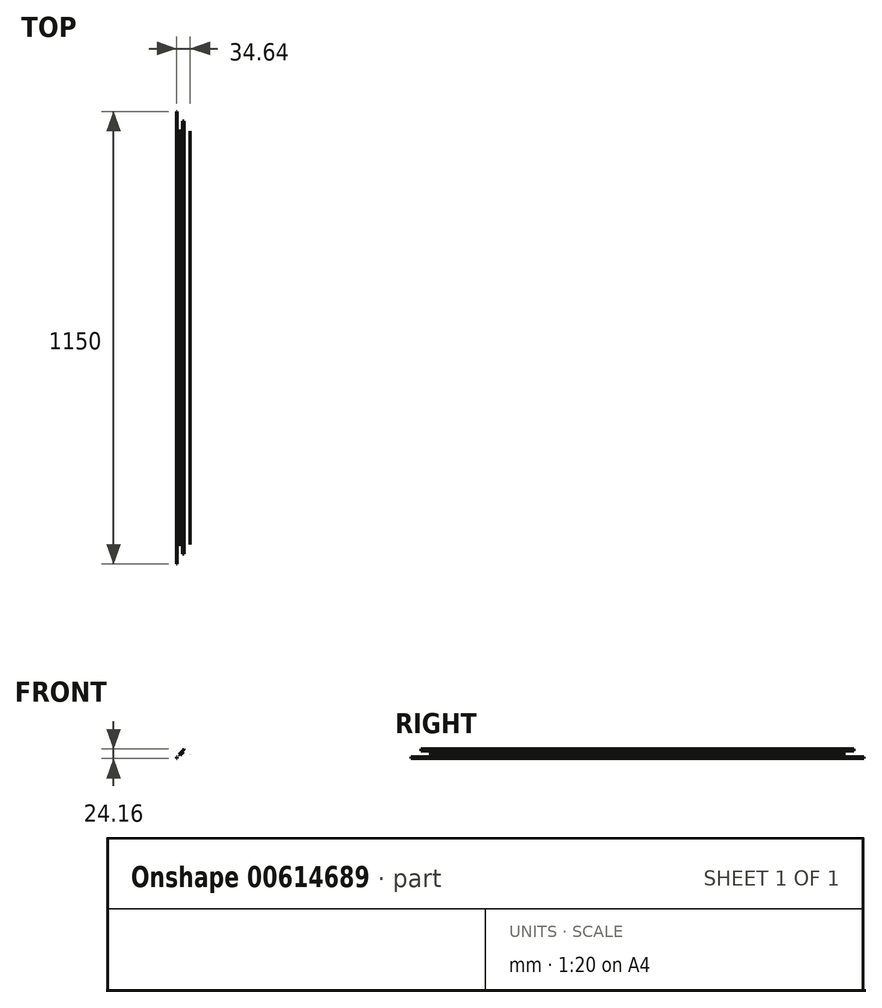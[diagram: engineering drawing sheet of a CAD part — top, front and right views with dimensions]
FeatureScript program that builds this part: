
annotation { "Feature Type Name" : "Feature", "Feature Type Description" : "" }
export const myFeature = defineFeature(function(context is Context, id is Id, definition is map)
    precondition{}
    {
        {
            var Q0;
            Q0=qCreatedBy(makeId("Front.planeOp"),FACE);
            var sketch = newSketch(context, id + "F0", { "sketchPlane" : qUnion([Q0])});
            skLineSegment(sketch, "E0.top", {"start": v(-22.5, -22.5) * mm, "end": v(22.5, -22.5) * mm, "construction": true});
            skLineSegment(sketch, "E0.left", {"start": v(-22.5, 22.5) * mm, "end": v(-22.5, -17.5) * mm, "construction": true});
            skLineSegment(sketch, "E0.right", {"start": v(22.5, 22.5) * mm, "end": v(22.5, -22.5) * mm, "construction": true});
            skPoint(sketch, "E0.middle", {"position": v(0, 0) * mm});
            skLineSegment(sketch, "E1", {"start": v(0, 0) * mm, "end": v(0, 21.4) * mm, "construction": true});
            skLineSegment(sketch, "E2", {"start": v(0, 0) * mm, "end": v(-11.87, 0) * mm, "construction": true});
            skLineSegment(sketch, "E3", {"start": v(0, 0) * mm, "end": v(6.41, 0) * mm, "construction": true});
            skLineSegment(sketch, "E4.top", {"start": v(-17.5, -17.5) * mm, "end": v(17.5, -17.5) * mm, "construction": true});
            skLineSegment(sketch, "E4.left", {"start": v(-17.5, 17.5) * mm, "end": v(-17.5, -14.52) * mm, "construction": true});
            skLineSegment(sketch, "E4.right", {"start": v(17.5, 17.5) * mm, "end": v(17.5, -14.52) * mm, "construction": true});
            skLineSegment(sketch, "E5.top", {"start": v(-19.5, -17.5) * mm, "end": v(22.5, -17.5) * mm, "construction": true});
            skLineSegment(sketch, "E5.left", {"start": v(-22.5, -22.5) * mm, "end": v(-22.5, -17.5) * mm, "construction": true});
            skLineSegment(sketch, "E5.right", {"start": v(22.5, -22.5) * mm, "end": v(22.5, -17.5) * mm, "construction": true});
            skLineSegment(sketch, "E6", {"start": v(-17.5, -17.5) * mm, "end": v(0, 0) * mm, "construction": true});
            skLineSegment(sketch, "E7", {"start": v(0, 0) * mm, "end": v(17.5, -17.5) * mm, "construction": true});
            skLineSegment(sketch, "E8.bottom", {"start": v(17.5, -17.5) * mm, "end": v(17.5, -17.5) * mm, "construction": true});
            skLineSegment(sketch, "E8.left", {"start": v(-17.5, -17.5) * mm, "end": v(-17.5, -22.5) * mm, "construction": true});
            skLineSegment(sketch, "E9.top", {"start": v(-22.5, -12.5) * mm, "end": v(22.5, -12.5) * mm, "construction": true});
            skLineSegment(sketch, "E9.left", {"start": v(-22.5, -17.5) * mm, "end": v(-22.5, -12.5) * mm, "construction": true});
            skLineSegment(sketch, "E9.right", {"start": v(22.5, -17.5) * mm, "end": v(22.5, -12.5) * mm, "construction": true});
            skLineSegment(sketch, "E10.top", {"start": v(-22.5, 5) * mm, "end": v(22.5, 5) * mm, "construction": true});
            skLineSegment(sketch, "E10.left", {"start": v(-22.5, 0) * mm, "end": v(-22.5, 5) * mm, "construction": true});
            skLineSegment(sketch, "E10.right", {"start": v(22.5, 0) * mm, "end": v(22.5, 5) * mm, "construction": true});
            skLineSegment(sketch, "E11", {"start": v(0, 5) * mm, "end": v(-17.5, -12.5) * mm, "construction": true});
            skLineSegment(sketch, "E12", {"start": v(0, 5) * mm, "end": v(17.5, -12.5) * mm, "construction": true});
            skLineSegment(sketch, "E13", {"start": v(0, 5) * mm, "end": v(-14.14, -9.14) * mm});
            skLineSegment(sketch, "E14", {"start": v(0, 5) * mm, "end": v(14.14, -9.14) * mm});
            skLineSegment(sketch, "E15", {"start": v(-14.14, -9.14) * mm, "end": v(-14.85, -8.44) * mm});
            skLineSegment(sketch, "E16", {"start": v(-11.87, -5.46) * mm, "end": v(0, 6.41) * mm});
            skLineSegment(sketch, "E17", {"start": v(14.14, -9.14) * mm, "end": v(14.85, -8.44) * mm});
            skLineSegment(sketch, "E18", {"start": v(11.87, -5.46) * mm, "end": v(0, 6.41) * mm});
            skLineSegment(sketch, "E19", {"start": v(-14.14, -9.14) * mm, "end": v(-11.31, -11.97) * mm});
            skLineSegment(sketch, "E20", {"start": v(-11.31, -11.97) * mm, "end": v(-1.41, -2.07) * mm});
            skLineSegment(sketch, "E21", {"start": v(-1.41, -2.07) * mm, "end": v(-4.24, 0.76) * mm});
            skLineSegment(sketch, "E22", {"start": v(-4.24, 0.76) * mm, "end": v(-14.14, -9.14) * mm});
            skLineSegment(sketch, "E23", {"start": v(14.14, -9.14) * mm, "end": v(11.31, -11.97) * mm});
            skLineSegment(sketch, "E24", {"start": v(11.31, -11.97) * mm, "end": v(1.41, -2.07) * mm});
            skLineSegment(sketch, "E25", {"start": v(1.41, -2.07) * mm, "end": v(4.24, 0.76) * mm});
            skLineSegment(sketch, "E26", {"start": v(4.24, 0.76) * mm, "end": v(14.14, -9.14) * mm});
            skLineSegment(sketch, "E27.top", {"start": v(-17.5, -14.52) * mm, "end": v(17.5, -14.52) * mm, "construction": true});
            skLineSegment(sketch, "E27.left", {"start": v(-17.5, -17.5) * mm, "end": v(-17.5, -14.52) * mm, "construction": true});
            skLineSegment(sketch, "E27.right", {"start": v(17.5, -17.5) * mm, "end": v(17.5, -14.52) * mm, "construction": true});
            skLineSegment(sketch, "E28.bottom", {"start": v(-14.85, -8.44) * mm, "end": v(14.85, -8.44) * mm, "construction": true});
            skLineSegment(sketch, "E28.top", {"start": v(-14.85, -14.52) * mm, "end": v(14.85, -14.52) * mm, "construction": true});
            skLineSegment(sketch, "E28.left", {"start": v(-14.85, -8.44) * mm, "end": v(-14.85, -14.52) * mm, "construction": true});
            skLineSegment(sketch, "E28.right", {"start": v(14.85, -8.44) * mm, "end": v(14.85, -14.52) * mm, "construction": true});
            skLineSegment(sketch, "E29.top", {"start": v(-14.85, -5.46) * mm, "end": v(14.85, -5.46) * mm, "construction": true});
            skLineSegment(sketch, "E29.left", {"start": v(-14.85, -8.44) * mm, "end": v(-14.85, -5.46) * mm, "construction": true});
            skLineSegment(sketch, "E29.right", {"start": v(14.85, -8.44) * mm, "end": v(14.85, -5.46) * mm, "construction": true});
            skLineSegment(sketch, "E30.top", {"start": v(-14.85, 0) * mm, "end": v(6.41, 0) * mm, "construction": true});
            skLineSegment(sketch, "E30.left", {"start": v(-14.85, -5.46) * mm, "end": v(-14.85, 0) * mm, "construction": true});
            skLineSegment(sketch, "E30.right", {"start": v(14.85, -5.46) * mm, "end": v(14.85, 0) * mm, "construction": true});
            skLineSegment(sketch, "E31.bottom", {"start": v(-11.87, -5.46) * mm, "end": v(11.85, -5.46) * mm, "construction": true});
            skLineSegment(sketch, "E31.top", {"start": v(-6.41, 0) * mm, "end": v(6.41, 0) * mm, "construction": true});
            skLineSegment(sketch, "E31.left", {"start": v(-11.87, -5.46) * mm, "end": v(-11.87, 0) * mm, "construction": true});
            skLineSegment(sketch, "E31.right", {"start": v(11.85, -5.46) * mm, "end": v(11.85, -5.44) * mm, "construction": true});
            skLineSegment(sketch, "E32.bottom", {"start": v(-6.41, 0) * mm, "end": v(-1.41, 0) * mm, "construction": true});
            skLineSegment(sketch, "E32.top", {"start": v(-6.41, 5) * mm, "end": v(-1.41, 5) * mm, "construction": true});
            skLineSegment(sketch, "E32.left", {"start": v(-6.41, 0) * mm, "end": v(-6.41, 5) * mm, "construction": true});
            skLineSegment(sketch, "E32.right", {"start": v(-1.41, 0) * mm, "end": v(-1.41, 5) * mm, "construction": true});
            skLineSegment(sketch, "E33.bottom", {"start": v(1.41, 5) * mm, "end": v(6.41, 5) * mm, "construction": true});
            skLineSegment(sketch, "E33.top", {"start": v(1.41, 0) * mm, "end": v(6.41, 0) * mm, "construction": true});
            skLineSegment(sketch, "E33.left", {"start": v(1.41, 5) * mm, "end": v(1.41, 0) * mm, "construction": true});
            skLineSegment(sketch, "E33.right", {"start": v(6.41, 5) * mm, "end": v(6.41, 0) * mm, "construction": true});
            skLineSegment(sketch, "E34.bottom", {"start": v(-1.41, 5) * mm, "end": v(1.41, 5) * mm, "construction": true});
            skLineSegment(sketch, "E34.top", {"start": v(-1.41, 0) * mm, "end": v(1.41, 0) * mm, "construction": true});
            skLineSegment(sketch, "E34.left", {"start": v(-1.41, 5) * mm, "end": v(-1.41, 0) * mm, "construction": true});
            skLineSegment(sketch, "E35", {"start": v(-22.5, -22.5) * mm, "end": v(-17.5, -22.5) * mm, "construction": true});
            skLineSegment(sketch, "E36", {"start": v(-17.5, -14.52) * mm, "end": v(-14.85, -14.52) * mm, "construction": true});
            skLineSegment(sketch, "E37", {"start": v(-6.41, 0) * mm, "end": v(0, 6.41) * mm});
            skLineSegment(sketch, "E38", {"start": v(14.85, -14.52) * mm, "end": v(17.5, -14.52) * mm});
            skLineSegment(sketch, "E39", {"start": v(-14.85, -8.44) * mm, "end": v(-11.87, -5.46) * mm});
            skLineSegment(sketch, "E40", {"start": v(0, 6.41) * mm, "end": v(6.41, 0) * mm});
            skLineSegment(sketch, "E41", {"start": v(11.85, -5.44) * mm, "end": v(11.85, -5.46) * mm});
            skPoint(sketch, "E42.start.orphan", {"position": v(29.54, 0) * mm});
            skLineSegment(sketch, "E43", {"start": v(0, 6.41) * mm, "end": v(-22.5, 6.41) * mm, "construction": true});
            skLineSegment(sketch, "E44", {"start": v(0, 6.41) * mm, "end": v(22.5, 6.41) * mm, "construction": true});
            skLineSegment(sketch, "E45", {"start": v(0, 6.41) * mm, "end": v(0, 21.38) * mm, "construction": true});
            skLineSegment(sketch, "E46.trimOffspring", {"start": v(-14.85, 0) * mm, "end": v(-22.5, 0) * mm, "construction": true});
            skLineSegment(sketch, "E47.trimOffspring", {"start": v(11.85, 0) * mm, "end": v(22.5, 0) * mm, "construction": true});
            skLineSegment(sketch, "E48.trimOffspring", {"start": v(11.85, 0) * mm, "end": v(14.85, 0) * mm, "construction": true});
            skLineSegment(sketch, "E49.bottom", {"start": v(22.5, -17.5) * mm, "end": v(-19.5, -17.5) * mm, "construction": true});
            skLineSegment(sketch, "E49.top", {"start": v(22.5, -19.5) * mm, "end": v(19.5, -19.5) * mm, "construction": true});
            skLineSegment(sketch, "E49.left", {"start": v(22.5, -17.5) * mm, "end": v(22.5, -19.5) * mm, "construction": true});
            skLineSegment(sketch, "E49.right", {"start": v(-22.5, -17.5) * mm, "end": v(-22.5, -19.5) * mm, "construction": true});
            skLineSegment(sketch, "E50.top", {"start": v(-22.5, 25.5) * mm, "end": v(-18.5, 25.5) * mm, "construction": true});
            skLineSegment(sketch, "E50.left", {"start": v(-22.5, 22.5) * mm, "end": v(-22.5, 25.5) * mm, "construction": true});
            skLineSegment(sketch, "E50.right", {"start": v(22.5, 22.5) * mm, "end": v(22.5, 25.5) * mm, "construction": true});
            skLineSegment(sketch, "E51.top", {"start": v(-22.5, -19.5) * mm, "end": v(17.5, -19.5) * mm, "construction": true});
            skLineSegment(sketch, "E51.left", {"start": v(-22.5, 25.5) * mm, "end": v(-22.5, -19.5) * mm, "construction": true});
            skLineSegment(sketch, "E51.right", {"start": v(22.5, 25.5) * mm, "end": v(22.5, -19.5) * mm, "construction": true});
            skLineSegment(sketch, "E52.bottom", {"start": v(-22.5, 6.41) * mm, "end": v(-18.5, 6.41) * mm, "construction": true});
            skLineSegment(sketch, "E52.top", {"start": v(-22.5, 28.72) * mm, "end": v(-18.5, 28.72) * mm, "construction": true});
            skLineSegment(sketch, "E52.left", {"start": v(-22.5, 6.41) * mm, "end": v(-22.5, 28.72) * mm, "construction": true});
            skLineSegment(sketch, "E52.right", {"start": v(-18.5, 22.5) * mm, "end": v(-18.5, 28.72) * mm, "construction": true});
            skLineSegment(sketch, "E53.bottom", {"start": v(22.5, 6.41) * mm, "end": v(18.5, 6.41) * mm, "construction": true});
            skLineSegment(sketch, "E53.top", {"start": v(22.5, 28.29) * mm, "end": v(18.5, 28.29) * mm, "construction": true});
            skLineSegment(sketch, "E53.left", {"start": v(22.5, 6.41) * mm, "end": v(22.5, 28.29) * mm, "construction": true});
            skLineSegment(sketch, "E53.right", {"start": v(18.5, 6.41) * mm, "end": v(18.5, 28.29) * mm, "construction": true});
            skLineSegment(sketch, "E54.bottom", {"start": v(-18.5, 6.41) * mm, "end": v(18.5, 6.41) * mm, "construction": true});
            skLineSegment(sketch, "E54.left", {"start": v(-18.5, 6.41) * mm, "end": v(-18.5, 21.4) * mm, "construction": true});
            skLineSegment(sketch, "E55.top", {"start": v(-18.5, 21.4) * mm, "end": v(18.5, 21.4) * mm, "construction": true});
            skLineSegment(sketch, "E55.right", {"start": v(18.5, 6.41) * mm, "end": v(18.5, 21.4) * mm, "construction": true});
            skPoint(sketch, "E56.orphan", {"position": v(0, 22.5) * mm});
            skLineSegment(sketch, "E57.bottom", {"start": v(-22.5, -19.5) * mm, "end": v(-24.5, -19.5) * mm, "construction": true});
            skLineSegment(sketch, "E57.top", {"start": v(-22.5, 25.5) * mm, "end": v(-24.5, 25.5) * mm, "construction": true});
            skLineSegment(sketch, "E57.left", {"start": v(-22.5, -19.5) * mm, "end": v(-22.5, 25.5) * mm, "construction": true});
            skLineSegment(sketch, "E57.right", {"start": v(-24.5, -19.5) * mm, "end": v(-24.5, 25.5) * mm, "construction": true});
            skLineSegment(sketch, "E58.bottom", {"start": v(22.5, -19.5) * mm, "end": v(24.5, -19.5) * mm, "construction": true});
            skLineSegment(sketch, "E58.top", {"start": v(22.5, 25.5) * mm, "end": v(24.5, 25.5) * mm, "construction": true});
            skLineSegment(sketch, "E58.left", {"start": v(22.5, -19.5) * mm, "end": v(22.5, 25.5) * mm, "construction": true});
            skLineSegment(sketch, "E58.right", {"start": v(24.5, -19.5) * mm, "end": v(24.5, 25.5) * mm, "construction": true});
            skLineSegment(sketch, "E59.bottom", {"start": v(-17.5, -17.5) * mm, "end": v(-19.5, -17.5) * mm, "construction": true});
            skLineSegment(sketch, "E59.top", {"start": v(-17.5, -14.52) * mm, "end": v(-19.5, -14.52) * mm, "construction": true});
            skLineSegment(sketch, "E59.right", {"start": v(-19.5, -17.5) * mm, "end": v(-19.5, -14.52) * mm, "construction": true});
            skLineSegment(sketch, "E60.bottom", {"start": v(17.5, -17.5) * mm, "end": v(19.5, -17.5) * mm, "construction": true});
            skLineSegment(sketch, "E60.top", {"start": v(17.5, -14.52) * mm, "end": v(19.5, -14.52) * mm, "construction": true});
            skLineSegment(sketch, "E60.right", {"start": v(19.5, -17.5) * mm, "end": v(19.5, -14.52) * mm, "construction": true});
            skLineSegment(sketch, "E61", {"start": v(-22.5, 6.41) * mm, "end": v(-24.5, 6.41) * mm, "construction": true});
            skLineSegment(sketch, "E62", {"start": v(22.5, 6.41) * mm, "end": v(24.5, 6.41) * mm, "construction": true});
            skLineSegment(sketch, "E63.bottom", {"start": v(-22.5, -19.5) * mm, "end": v(-19.5, -19.5) * mm, "construction": true});
            skLineSegment(sketch, "E63.top", {"start": v(-22.5, -17.5) * mm, "end": v(-19.5, -17.5) * mm, "construction": true});
            skLineSegment(sketch, "E63.left", {"start": v(-22.5, -19.5) * mm, "end": v(-22.5, -17.5) * mm, "construction": true});
            skLineSegment(sketch, "E63.right", {"start": v(-19.5, -19.5) * mm, "end": v(-19.5, -17.5) * mm, "construction": true});
            skLineSegment(sketch, "E64.top", {"start": v(22.5, -17.5) * mm, "end": v(19.5, -17.5) * mm, "construction": true});
            skLineSegment(sketch, "E64.left", {"start": v(22.5, -19.5) * mm, "end": v(22.5, -17.5) * mm, "construction": true});
            skLineSegment(sketch, "E64.right", {"start": v(19.5, -19.5) * mm, "end": v(19.5, -17.5) * mm, "construction": true});
            skLineSegment(sketch, "E65.bottom", {"start": v(-18.5, 21.4) * mm, "end": v(-24.5, 21.4) * mm, "construction": true});
            skLineSegment(sketch, "E65.top", {"start": v(-18.5, 25.5) * mm, "end": v(-24.5, 25.5) * mm, "construction": true});
            skLineSegment(sketch, "E65.left", {"start": v(-18.5, 21.4) * mm, "end": v(-18.5, 25.5) * mm, "construction": true});
            skLineSegment(sketch, "E65.right", {"start": v(-24.5, 21.4) * mm, "end": v(-24.5, 25.5) * mm, "construction": true});
            skLineSegment(sketch, "E66.bottom", {"start": v(18.5, 21.4) * mm, "end": v(24.5, 21.4) * mm, "construction": true});
            skLineSegment(sketch, "E66.left", {"start": v(18.5, 21.4) * mm, "end": v(18.5, 25.5) * mm, "construction": true});
            skLineSegment(sketch, "E66.right", {"start": v(24.5, 21.4) * mm, "end": v(24.5, 25.5) * mm, "construction": true});
            skLineSegment(sketch, "E67", {"start": v(-24.5, 6.41) * mm, "end": v(-24.5, -17.57) * mm});
            skLineSegment(sketch, "E68", {"start": v(-19.5, -17.5) * mm, "end": v(-19.5, -14.52) * mm});
            skLineSegment(sketch, "E69", {"start": v(-19.5, -14.52) * mm, "end": v(-14.85, -14.52) * mm});
            skLineSegment(sketch, "E70", {"start": v(-14.85, -14.52) * mm, "end": v(-14.85, -8.44) * mm});
            skLineSegment(sketch, "E71", {"start": v(-11.87, -5.46) * mm, "end": v(-11.87, 0) * mm});
            skLineSegment(sketch, "E72", {"start": v(-11.87, 0) * mm, "end": v(-6.41, 0) * mm});
            skLineSegment(sketch, "E73", {"start": v(11.85, -5.44) * mm, "end": v(11.87, -5.46) * mm});
            skLineSegment(sketch, "E74", {"start": v(14.85, -8.44) * mm, "end": v(14.85, -14.06) * mm});
            skLineSegment(sketch, "E75", {"start": v(14.85, -14.06) * mm, "end": v(14.85, -14.52) * mm});
            skLineSegment(sketch, "E76", {"start": v(17.5, -14.52) * mm, "end": v(17.5, -17.5) * mm});
            skLineSegment(sketch, "E77", {"start": v(17.5, -19.5) * mm, "end": v(22.5, -19.5) * mm});
            skLineSegment(sketch, "E78", {"start": v(22.5, -19.5) * mm, "end": v(22.5, 6.41) * mm});
            skLineSegment(sketch, "E79", {"start": v(18.5, 25.5) * mm, "end": v(-22.5, 25.5) * mm});
            skLineSegment(sketch, "E80", {"start": v(-24.5, -17.57) * mm, "end": v(-24.5, -19.5) * mm});
            skLineSegment(sketch, "E81", {"start": v(-24.5, -19.5) * mm, "end": v(-19.5, -19.5) * mm});
            skLineSegment(sketch, "E82", {"start": v(-19.5, -19.5) * mm, "end": v(-19.5, -17.5) * mm});
            skLineSegment(sketch, "E83", {"start": v(18.5, 25.5) * mm, "end": v(22.5, 25.5) * mm});
            skLineSegment(sketch, "E84", {"start": v(24.5, 6.41) * mm, "end": v(24.5, -19.5) * mm});
            skLineSegment(sketch, "E85", {"start": v(24.5, -19.5) * mm, "end": v(22.5, -19.5) * mm});
            skLineSegment(sketch, "E86.trimOffspring", {"start": v(17.5, -19.5) * mm, "end": v(-22.5, -19.5) * mm, "construction": true});
            skLineSegment(sketch, "E87", {"start": v(14.85, -14.52) * mm, "end": v(19.5, -14.52) * mm});
            skLineSegment(sketch, "E88", {"start": v(19.5, -14.52) * mm, "end": v(19.5, -19.5) * mm});
            skLineSegment(sketch, "E89", {"start": v(19.5, -19.5) * mm, "end": v(24.5, -19.5) * mm});
            skLineSegment(sketch, "E90.trimOffspring", {"start": v(19.5, -19.5) * mm, "end": v(22.5, -19.5) * mm, "construction": true});
            skLineSegment(sketch, "E91.bottom", {"start": v(-24.5, 25.5) * mm, "end": v(24.5, 25.5) * mm, "construction": true});
            skLineSegment(sketch, "E91.top", {"start": v(-24.5, 0) * mm, "end": v(6.41, 0) * mm, "construction": true});
            skLineSegment(sketch, "E91.left", {"start": v(-24.5, 25.5) * mm, "end": v(-24.5, 0) * mm, "construction": true});
            skLineSegment(sketch, "E91.right", {"start": v(24.5, 25.5) * mm, "end": v(24.5, 0) * mm, "construction": true});
            skLineSegment(sketch, "E92", {"start": v(-22.5, 25.5) * mm, "end": v(-24.5, 0) * mm});
            skLineSegment(sketch, "E93", {"start": v(22.5, 25.5) * mm, "end": v(24.5, 0) * mm});
            skLineSegment(sketch, "E94.top", {"start": v(-22.5, 29.5) * mm, "end": v(22.5, 29.5) * mm, "construction": true});
            skLineSegment(sketch, "E94.left", {"start": v(-22.5, 25.5) * mm, "end": v(-22.5, 29.5) * mm, "construction": true});
            skLineSegment(sketch, "E94.right", {"start": v(22.5, 25.5) * mm, "end": v(22.5, 29.5) * mm, "construction": true});
            skLineSegment(sketch, "E95", {"start": v(-22.5, 25.5) * mm, "end": v(-18.5, 29.5) * mm});
            skLineSegment(sketch, "E96", {"start": v(22.5, 25.5) * mm, "end": v(18.49, 29.5) * mm});
            skLineSegment(sketch, "E97", {"start": v(18.49, 29.5) * mm, "end": v(-18.94, 29.5) * mm});
            skLineSegment(sketch, "E98.trimOffspring", {"start": v(18.5, 25.5) * mm, "end": v(22.5, 25.5) * mm, "construction": true});
            skLineSegment(sketch, "E99", {"start": v(11.85, -5.44) * mm, "end": v(14.85, -8.44) * mm});
            skLineSegment(sketch, "E100", {"start": v(14.85, -8.44) * mm, "end": v(14.85, -14.52) * mm});
            skLineSegment(sketch, "E101.trimOffspring", {"start": v(11.85, 0) * mm, "end": v(24.5, 0) * mm, "construction": true});
            skLineSegment(sketch, "E102", {"start": v(14.85, -8.44) * mm, "end": v(11.87, -5.46) * mm});
            skLineSegment(sketch, "E103", {"start": v(11.87, -5.46) * mm, "end": v(11.85, 0) * mm});
            skLineSegment(sketch, "E104", {"start": v(11.85, 0) * mm, "end": v(6.41, 0) * mm});
            skLineSegment(sketch, "E105", {"start": v(6.41, 0) * mm, "end": v(1.41, 5) * mm});
            skLineSegment(sketch, "E106.bottom", {"start": v(0, 6.41) * mm, "end": v(-1.41, 6.41) * mm, "construction": true});
            skLineSegment(sketch, "E106.top", {"start": v(0, 5) * mm, "end": v(-1.41, 5) * mm, "construction": true});
            skLineSegment(sketch, "E106.left", {"start": v(0, 6.41) * mm, "end": v(0, 5) * mm, "construction": true});
            skLineSegment(sketch, "E106.right", {"start": v(-1.41, 6.41) * mm, "end": v(-1.41, 5) * mm, "construction": true});
            skLineSegment(sketch, "E107.bottom", {"start": v(0, 6.41) * mm, "end": v(1.41, 6.41) * mm, "construction": true});
            skLineSegment(sketch, "E107.top", {"start": v(0, 5) * mm, "end": v(1.41, 5) * mm, "construction": true});
            skLineSegment(sketch, "E107.right", {"start": v(1.41, 6.41) * mm, "end": v(1.41, 5) * mm, "construction": true});
            skLineSegment(sketch, "E108.bottom", {"start": v(-1.41, 6.41) * mm, "end": v(1.41, 6.41) * mm, "construction": true});
            skLineSegment(sketch, "E108.top", {"start": v(-1.41, 21.4) * mm, "end": v(1.41, 21.4) * mm, "construction": true});
            skLineSegment(sketch, "E108.left", {"start": v(-1.41, 6.41) * mm, "end": v(-1.41, 21.4) * mm, "construction": true});
            skLineSegment(sketch, "E108.right", {"start": v(1.41, 6.41) * mm, "end": v(1.41, 21.4) * mm, "construction": true});
            skLineSegment(sketch, "E109.bottom", {"start": v(1.41, 21.4) * mm, "end": v(-1.41, 21.4) * mm, "construction": true});
            skLineSegment(sketch, "E109.top", {"start": v(1.41, 29.5) * mm, "end": v(-1.41, 29.5) * mm, "construction": true});
            skLineSegment(sketch, "E109.left", {"start": v(1.41, 21.4) * mm, "end": v(1.41, 29.5) * mm, "construction": true});
            skLineSegment(sketch, "E109.right", {"start": v(-1.41, 21.4) * mm, "end": v(-1.41, 29.5) * mm, "construction": true});
            skLineSegment(sketch, "E110", {"start": v(0, 29.5) * mm, "end": v(0, 21.4) * mm});
            skLineSegment(sketch, "E111", {"start": v(0, 21.4) * mm, "end": v(0, 6.41) * mm});
            skLineSegment(sketch, "E112", {"start": v(0, 6.41) * mm, "end": v(-1.41, 6.41) * mm});
            skLineSegment(sketch, "E113", {"start": v(-1.41, 6.41) * mm, "end": v(-1.41, 5) * mm});
            skLineSegment(sketch, "E114", {"start": v(0, 6.41) * mm, "end": v(1.41, 6.41) * mm});
            skLineSegment(sketch, "E115", {"start": v(1.41, 6.41) * mm, "end": v(1.41, 5) * mm});
            skLineSegment(sketch, "E116.top", {"start": v(-23.5, -22.85) * mm, "end": v(21.5, -22.85) * mm, "construction": true});
            skLineSegment(sketch, "E116.left", {"start": v(-23.5, 22.15) * mm, "end": v(-23.5, -17.85) * mm, "construction": true});
            skLineSegment(sketch, "E116.right", {"start": v(21.5, 22.15) * mm, "end": v(21.5, -22.85) * mm, "construction": true});
            skPoint(sketch, "E116.middle", {"position": v(-1, -0.35) * mm});
            skLineSegment(sketch, "E117", {"start": v(-1, -0.35) * mm, "end": v(-1, 21.04) * mm, "construction": true});
            skLineSegment(sketch, "E118", {"start": v(-1, -0.35) * mm, "end": v(-12.87, -0.35) * mm, "construction": true});
            skLineSegment(sketch, "E119", {"start": v(-1, -0.35) * mm, "end": v(5.42, -0.35) * mm, "construction": true});
            skLineSegment(sketch, "E120.top", {"start": v(-18.5, -17.85) * mm, "end": v(16.5, -17.85) * mm, "construction": true});
            skLineSegment(sketch, "E120.left", {"start": v(-18.5, 17.15) * mm, "end": v(-18.5, -14.87) * mm, "construction": true});
            skLineSegment(sketch, "E120.right", {"start": v(16.5, 17.15) * mm, "end": v(16.5, -14.87) * mm, "construction": true});
            skLineSegment(sketch, "E121.top", {"start": v(-20.5, -17.85) * mm, "end": v(21.5, -17.85) * mm, "construction": true});
            skLineSegment(sketch, "E121.left", {"start": v(-23.5, -22.85) * mm, "end": v(-23.5, -17.85) * mm, "construction": true});
            skLineSegment(sketch, "E121.right", {"start": v(21.5, -22.85) * mm, "end": v(21.5, -17.85) * mm, "construction": true});
            skLineSegment(sketch, "E122", {"start": v(-18.5, -17.85) * mm, "end": v(-1, -0.35) * mm, "construction": true});
            skLineSegment(sketch, "E123", {"start": v(-1, -0.35) * mm, "end": v(16.5, -17.85) * mm, "construction": true});
            skLineSegment(sketch, "E124.bottom", {"start": v(16.5, -17.85) * mm, "end": v(16.5, -17.85) * mm, "construction": true});
            skLineSegment(sketch, "E124.left", {"start": v(-18.5, -17.85) * mm, "end": v(-18.5, -22.85) * mm, "construction": true});
            skLineSegment(sketch, "E125.top", {"start": v(-23.5, -12.85) * mm, "end": v(21.5, -12.85) * mm, "construction": true});
            skLineSegment(sketch, "E125.left", {"start": v(-23.5, -17.85) * mm, "end": v(-23.5, -12.85) * mm, "construction": true});
            skLineSegment(sketch, "E125.right", {"start": v(21.5, -17.85) * mm, "end": v(21.5, -12.85) * mm, "construction": true});
            skLineSegment(sketch, "E126.top", {"start": v(-23.5, 4.65) * mm, "end": v(21.5, 4.65) * mm, "construction": true});
            skLineSegment(sketch, "E126.left", {"start": v(-23.5, -0.35) * mm, "end": v(-23.5, 4.65) * mm, "construction": true});
            skLineSegment(sketch, "E126.right", {"start": v(21.5, -0.35) * mm, "end": v(21.5, 4.65) * mm, "construction": true});
            skLineSegment(sketch, "E127", {"start": v(-1, 4.65) * mm, "end": v(-18.5, -12.85) * mm, "construction": true});
            skLineSegment(sketch, "E128", {"start": v(-1, 4.65) * mm, "end": v(16.5, -12.85) * mm, "construction": true});
            skLineSegment(sketch, "E129", {"start": v(-1, 4.65) * mm, "end": v(-15.14, -9.5) * mm});
            skLineSegment(sketch, "E130", {"start": v(-1, 4.65) * mm, "end": v(13.14, -9.5) * mm});
            skLineSegment(sketch, "E131", {"start": v(-15.14, -9.5) * mm, "end": v(-15.85, -8.79) * mm});
            skLineSegment(sketch, "E132", {"start": v(-12.87, -5.81) * mm, "end": v(-1, 6.06) * mm});
            skLineSegment(sketch, "E133", {"start": v(13.14, -9.5) * mm, "end": v(13.85, -8.79) * mm});
            skLineSegment(sketch, "E134", {"start": v(10.87, -5.81) * mm, "end": v(-1, 6.06) * mm});
            skLineSegment(sketch, "E135", {"start": v(-15.14, -9.5) * mm, "end": v(-12.31, -12.32) * mm});
            skLineSegment(sketch, "E136", {"start": v(-12.31, -12.32) * mm, "end": v(-2.41, -2.42) * mm});
            skLineSegment(sketch, "E137", {"start": v(-2.41, -2.42) * mm, "end": v(-5.24, 0.4) * mm});
            skLineSegment(sketch, "E138", {"start": v(-5.24, 0.4) * mm, "end": v(-15.14, -9.5) * mm});
            skLineSegment(sketch, "E139", {"start": v(13.14, -9.5) * mm, "end": v(10.32, -12.32) * mm});
            skLineSegment(sketch, "E140", {"start": v(10.32, -12.32) * mm, "end": v(0.42, -2.42) * mm});
            skLineSegment(sketch, "E141", {"start": v(0.42, -2.42) * mm, "end": v(3.24, 0.4) * mm});
            skLineSegment(sketch, "E142", {"start": v(3.24, 0.4) * mm, "end": v(13.14, -9.5) * mm});
            skLineSegment(sketch, "E143.top", {"start": v(-18.5, -14.87) * mm, "end": v(16.5, -14.87) * mm, "construction": true});
            skLineSegment(sketch, "E143.left", {"start": v(-18.5, -17.85) * mm, "end": v(-18.5, -14.87) * mm, "construction": true});
            skLineSegment(sketch, "E143.right", {"start": v(16.5, -17.85) * mm, "end": v(16.5, -14.87) * mm, "construction": true});
            skLineSegment(sketch, "E144.bottom", {"start": v(-15.85, -8.79) * mm, "end": v(13.85, -8.79) * mm, "construction": true});
            skLineSegment(sketch, "E144.top", {"start": v(-15.85, -14.87) * mm, "end": v(13.85, -14.87) * mm, "construction": true});
            skLineSegment(sketch, "E144.left", {"start": v(-15.85, -8.79) * mm, "end": v(-15.85, -14.87) * mm, "construction": true});
            skLineSegment(sketch, "E144.right", {"start": v(13.85, -8.79) * mm, "end": v(13.85, -14.87) * mm, "construction": true});
            skLineSegment(sketch, "E145.top", {"start": v(-15.85, -5.81) * mm, "end": v(13.85, -5.81) * mm, "construction": true});
            skLineSegment(sketch, "E145.left", {"start": v(-15.85, -8.79) * mm, "end": v(-15.85, -5.81) * mm, "construction": true});
            skLineSegment(sketch, "E145.right", {"start": v(13.85, -8.79) * mm, "end": v(13.85, -5.81) * mm, "construction": true});
            skLineSegment(sketch, "E146.top", {"start": v(-15.85, -0.35) * mm, "end": v(5.42, -0.35) * mm, "construction": true});
            skLineSegment(sketch, "E146.left", {"start": v(-15.85, -5.81) * mm, "end": v(-15.85, -0.35) * mm, "construction": true});
            skLineSegment(sketch, "E146.right", {"start": v(13.85, -5.81) * mm, "end": v(13.85, -0.35) * mm, "construction": true});
            skLineSegment(sketch, "E147.bottom", {"start": v(-12.87, -5.81) * mm, "end": v(10.85, -5.81) * mm, "construction": true});
            skLineSegment(sketch, "E147.top", {"start": v(-7.41, -0.35) * mm, "end": v(5.42, -0.35) * mm, "construction": true});
            skLineSegment(sketch, "E147.left", {"start": v(-12.87, -5.81) * mm, "end": v(-12.87, -0.35) * mm, "construction": true});
            skLineSegment(sketch, "E147.right", {"start": v(10.85, -5.81) * mm, "end": v(10.85, -5.79) * mm, "construction": true});
            skLineSegment(sketch, "E148.bottom", {"start": v(-7.41, -0.35) * mm, "end": v(-2.41, -0.35) * mm, "construction": true});
            skLineSegment(sketch, "E148.top", {"start": v(-7.41, 4.65) * mm, "end": v(-2.41, 4.65) * mm, "construction": true});
            skLineSegment(sketch, "E148.left", {"start": v(-7.41, -0.35) * mm, "end": v(-7.41, 4.65) * mm, "construction": true});
            skLineSegment(sketch, "E148.right", {"start": v(-2.41, -0.35) * mm, "end": v(-2.41, 4.65) * mm, "construction": true});
            skLineSegment(sketch, "E149.bottom", {"start": v(0.42, 4.65) * mm, "end": v(5.42, 4.65) * mm, "construction": true});
            skLineSegment(sketch, "E149.top", {"start": v(0.42, -0.35) * mm, "end": v(5.42, -0.35) * mm, "construction": true});
            skLineSegment(sketch, "E149.left", {"start": v(0.42, 4.65) * mm, "end": v(0.42, -0.35) * mm, "construction": true});
            skLineSegment(sketch, "E149.right", {"start": v(5.42, 4.65) * mm, "end": v(5.42, -0.35) * mm, "construction": true});
            skLineSegment(sketch, "E150.bottom", {"start": v(-2.41, 4.65) * mm, "end": v(0.42, 4.65) * mm, "construction": true});
            skLineSegment(sketch, "E150.top", {"start": v(-2.41, -0.35) * mm, "end": v(0.42, -0.35) * mm, "construction": true});
            skLineSegment(sketch, "E150.left", {"start": v(-2.41, 4.65) * mm, "end": v(-2.41, -0.35) * mm, "construction": true});
            skLineSegment(sketch, "E151", {"start": v(-23.5, -22.85) * mm, "end": v(-18.5, -22.85) * mm, "construction": true});
            skLineSegment(sketch, "E152", {"start": v(-18.5, -14.87) * mm, "end": v(-15.85, -14.87) * mm, "construction": true});
            skLineSegment(sketch, "E153", {"start": v(-7.41, -0.35) * mm, "end": v(-1, 6.06) * mm});
            skLineSegment(sketch, "E154", {"start": v(13.85, -14.87) * mm, "end": v(16.5, -14.87) * mm});
            skLineSegment(sketch, "E155", {"start": v(-15.85, -8.79) * mm, "end": v(-12.87, -5.81) * mm});
            skLineSegment(sketch, "E156", {"start": v(-1, 6.06) * mm, "end": v(5.42, -0.35) * mm});
            skLineSegment(sketch, "E157", {"start": v(10.85, -5.79) * mm, "end": v(10.85, -5.81) * mm});
            skPoint(sketch, "E158.start.orphan", {"position": v(28.54, -0.35) * mm});
            skLineSegment(sketch, "E159", {"start": v(-1, 6.06) * mm, "end": v(-23.5, 6.06) * mm, "construction": true});
            skLineSegment(sketch, "E160", {"start": v(-1, 6.06) * mm, "end": v(21.5, 6.06) * mm, "construction": true});
            skLineSegment(sketch, "E161", {"start": v(-1, 6.06) * mm, "end": v(-1, 21.03) * mm, "construction": true});
            skLineSegment(sketch, "E162.trimOffspring", {"start": v(-15.85, -0.35) * mm, "end": v(-23.5, -0.35) * mm, "construction": true});
            skLineSegment(sketch, "E163.trimOffspring", {"start": v(10.85, -0.35) * mm, "end": v(21.5, -0.35) * mm, "construction": true});
            skLineSegment(sketch, "E164.trimOffspring", {"start": v(10.85, -0.35) * mm, "end": v(13.85, -0.35) * mm, "construction": true});
            skLineSegment(sketch, "E165.bottom", {"start": v(21.5, -17.85) * mm, "end": v(-20.5, -17.85) * mm, "construction": true});
            skLineSegment(sketch, "E165.top", {"start": v(21.5, -19.86) * mm, "end": v(18.5, -19.86) * mm, "construction": true});
            skLineSegment(sketch, "E165.left", {"start": v(21.5, -17.85) * mm, "end": v(21.5, -19.86) * mm, "construction": true});
            skLineSegment(sketch, "E165.right", {"start": v(-23.5, -17.85) * mm, "end": v(-23.5, -19.86) * mm, "construction": true});
            skLineSegment(sketch, "E166.top", {"start": v(-23.5, 25.14) * mm, "end": v(-19.5, 25.14) * mm, "construction": true});
            skLineSegment(sketch, "E166.left", {"start": v(-23.5, 22.15) * mm, "end": v(-23.5, 25.14) * mm, "construction": true});
            skLineSegment(sketch, "E166.right", {"start": v(21.5, 22.15) * mm, "end": v(21.5, 25.14) * mm, "construction": true});
            skLineSegment(sketch, "E167.top", {"start": v(-23.5, -19.86) * mm, "end": v(16.5, -19.86) * mm, "construction": true});
            skLineSegment(sketch, "E167.left", {"start": v(-23.5, 25.14) * mm, "end": v(-23.5, -19.86) * mm, "construction": true});
            skLineSegment(sketch, "E167.right", {"start": v(21.5, 25.14) * mm, "end": v(21.5, -19.86) * mm, "construction": true});
            skLineSegment(sketch, "E168.bottom", {"start": v(-23.5, 6.06) * mm, "end": v(-19.5, 6.06) * mm, "construction": true});
            skLineSegment(sketch, "E168.top", {"start": v(-23.5, 28.37) * mm, "end": v(-19.5, 28.37) * mm, "construction": true});
            skLineSegment(sketch, "E168.left", {"start": v(-23.5, 6.06) * mm, "end": v(-23.5, 28.37) * mm, "construction": true});
            skLineSegment(sketch, "E168.right", {"start": v(-19.5, 22.15) * mm, "end": v(-19.5, 28.37) * mm, "construction": true});
            skLineSegment(sketch, "E169.bottom", {"start": v(21.5, 6.06) * mm, "end": v(17.5, 6.06) * mm, "construction": true});
            skLineSegment(sketch, "E169.top", {"start": v(21.5, 27.93) * mm, "end": v(17.5, 27.93) * mm, "construction": true});
            skLineSegment(sketch, "E169.left", {"start": v(21.5, 6.06) * mm, "end": v(21.5, 27.93) * mm, "construction": true});
            skLineSegment(sketch, "E169.right", {"start": v(17.5, 6.06) * mm, "end": v(17.5, 27.93) * mm, "construction": true});
            skLineSegment(sketch, "E170.bottom", {"start": v(-19.5, 6.06) * mm, "end": v(17.5, 6.06) * mm, "construction": true});
            skLineSegment(sketch, "E170.left", {"start": v(-19.5, 6.06) * mm, "end": v(-19.5, 21.04) * mm, "construction": true});
            skLineSegment(sketch, "E171.top", {"start": v(-19.5, 21.04) * mm, "end": v(17.5, 21.04) * mm, "construction": true});
            skLineSegment(sketch, "E171.right", {"start": v(17.5, 6.06) * mm, "end": v(17.5, 21.04) * mm, "construction": true});
            skPoint(sketch, "E172.orphan", {"position": v(-1, 22.15) * mm});
            skLineSegment(sketch, "E173.bottom", {"start": v(-23.5, -19.86) * mm, "end": v(-25.5, -19.86) * mm, "construction": true});
            skLineSegment(sketch, "E173.top", {"start": v(-23.5, 25.14) * mm, "end": v(-25.5, 25.14) * mm, "construction": true});
            skLineSegment(sketch, "E173.left", {"start": v(-23.5, -19.86) * mm, "end": v(-23.5, 25.14) * mm, "construction": true});
            skLineSegment(sketch, "E173.right", {"start": v(-25.5, -19.86) * mm, "end": v(-25.5, 25.14) * mm, "construction": true});
            skLineSegment(sketch, "E174.bottom", {"start": v(21.5, -19.86) * mm, "end": v(23.5, -19.86) * mm, "construction": true});
            skLineSegment(sketch, "E174.top", {"start": v(21.5, 25.14) * mm, "end": v(23.5, 25.14) * mm, "construction": true});
            skLineSegment(sketch, "E174.left", {"start": v(21.5, -19.86) * mm, "end": v(21.5, 25.14) * mm, "construction": true});
            skLineSegment(sketch, "E174.right", {"start": v(23.5, -19.86) * mm, "end": v(23.5, 25.14) * mm, "construction": true});
            skLineSegment(sketch, "E175.bottom", {"start": v(-18.5, -17.85) * mm, "end": v(-20.5, -17.85) * mm, "construction": true});
            skLineSegment(sketch, "E175.top", {"start": v(-18.5, -14.87) * mm, "end": v(-20.5, -14.87) * mm, "construction": true});
            skLineSegment(sketch, "E175.right", {"start": v(-20.5, -17.85) * mm, "end": v(-20.5, -14.87) * mm, "construction": true});
            skLineSegment(sketch, "E176.bottom", {"start": v(16.5, -17.85) * mm, "end": v(18.5, -17.85) * mm, "construction": true});
            skLineSegment(sketch, "E176.top", {"start": v(16.5, -14.87) * mm, "end": v(18.5, -14.87) * mm, "construction": true});
            skLineSegment(sketch, "E176.right", {"start": v(18.5, -17.85) * mm, "end": v(18.5, -14.87) * mm, "construction": true});
            skLineSegment(sketch, "E177", {"start": v(-23.5, 6.06) * mm, "end": v(-25.5, 6.06) * mm, "construction": true});
            skLineSegment(sketch, "E178", {"start": v(21.5, 6.06) * mm, "end": v(23.5, 6.06) * mm, "construction": true});
            skLineSegment(sketch, "E179.bottom", {"start": v(-23.5, -19.86) * mm, "end": v(-20.5, -19.86) * mm, "construction": true});
            skLineSegment(sketch, "E179.top", {"start": v(-23.5, -17.85) * mm, "end": v(-20.5, -17.85) * mm, "construction": true});
            skLineSegment(sketch, "E179.left", {"start": v(-23.5, -19.86) * mm, "end": v(-23.5, -17.85) * mm, "construction": true});
            skLineSegment(sketch, "E179.right", {"start": v(-20.5, -19.86) * mm, "end": v(-20.5, -17.85) * mm, "construction": true});
            skLineSegment(sketch, "E180.top", {"start": v(21.5, -17.85) * mm, "end": v(18.5, -17.85) * mm, "construction": true});
            skLineSegment(sketch, "E180.left", {"start": v(21.5, -19.86) * mm, "end": v(21.5, -17.85) * mm, "construction": true});
            skLineSegment(sketch, "E180.right", {"start": v(18.5, -19.86) * mm, "end": v(18.5, -17.85) * mm, "construction": true});
            skLineSegment(sketch, "E181.bottom", {"start": v(-19.5, 21.04) * mm, "end": v(-25.5, 21.04) * mm, "construction": true});
            skLineSegment(sketch, "E181.top", {"start": v(-19.5, 25.14) * mm, "end": v(-25.5, 25.14) * mm, "construction": true});
            skLineSegment(sketch, "E181.left", {"start": v(-19.5, 21.04) * mm, "end": v(-19.5, 25.14) * mm, "construction": true});
            skLineSegment(sketch, "E181.right", {"start": v(-25.5, 21.04) * mm, "end": v(-25.5, 25.14) * mm, "construction": true});
            skLineSegment(sketch, "E182.bottom", {"start": v(17.5, 21.04) * mm, "end": v(23.5, 21.04) * mm, "construction": true});
            skLineSegment(sketch, "E182.left", {"start": v(17.5, 21.04) * mm, "end": v(17.5, 25.14) * mm, "construction": true});
            skLineSegment(sketch, "E182.right", {"start": v(23.5, 21.04) * mm, "end": v(23.5, 25.14) * mm, "construction": true});
            skLineSegment(sketch, "E183", {"start": v(-25.5, 6.06) * mm, "end": v(-25.5, -17.92) * mm});
            skLineSegment(sketch, "E184", {"start": v(-20.5, -17.85) * mm, "end": v(-20.5, -14.87) * mm});
            skLineSegment(sketch, "E185", {"start": v(-20.5, -14.87) * mm, "end": v(-15.85, -14.87) * mm});
            skLineSegment(sketch, "E186", {"start": v(-15.85, -14.87) * mm, "end": v(-15.85, -8.79) * mm});
            skLineSegment(sketch, "E187", {"start": v(-12.87, -5.81) * mm, "end": v(-12.87, -0.35) * mm});
            skLineSegment(sketch, "E188", {"start": v(-12.87, -0.35) * mm, "end": v(-7.41, -0.35) * mm});
            skLineSegment(sketch, "E189", {"start": v(10.85, -5.79) * mm, "end": v(10.87, -5.81) * mm});
            skLineSegment(sketch, "E190", {"start": v(13.85, -8.79) * mm, "end": v(13.85, -14.41) * mm});
            skLineSegment(sketch, "E191", {"start": v(13.85, -14.41) * mm, "end": v(13.85, -14.87) * mm});
            skLineSegment(sketch, "E192", {"start": v(16.5, -14.87) * mm, "end": v(16.5, -17.85) * mm});
            skLineSegment(sketch, "E193", {"start": v(16.5, -19.86) * mm, "end": v(21.5, -19.86) * mm});
            skLineSegment(sketch, "E194", {"start": v(21.5, -19.86) * mm, "end": v(21.5, 6.06) * mm});
            skLineSegment(sketch, "E195", {"start": v(17.5, 25.14) * mm, "end": v(-23.5, 25.14) * mm});
            skLineSegment(sketch, "E196", {"start": v(-25.5, -17.92) * mm, "end": v(-25.5, -19.86) * mm});
            skLineSegment(sketch, "E197", {"start": v(-25.5, -19.86) * mm, "end": v(-20.5, -19.86) * mm});
            skLineSegment(sketch, "E198", {"start": v(-20.5, -19.86) * mm, "end": v(-20.5, -17.85) * mm});
            skLineSegment(sketch, "E199", {"start": v(17.5, 25.14) * mm, "end": v(21.5, 25.14) * mm});
            skLineSegment(sketch, "E200", {"start": v(23.5, 6.06) * mm, "end": v(23.5, -19.86) * mm});
            skLineSegment(sketch, "E201", {"start": v(23.5, -19.86) * mm, "end": v(21.5, -19.86) * mm});
            skLineSegment(sketch, "E202.trimOffspring", {"start": v(16.5, -19.86) * mm, "end": v(-23.5, -19.86) * mm, "construction": true});
            skLineSegment(sketch, "E203", {"start": v(13.85, -14.87) * mm, "end": v(18.5, -14.87) * mm});
            skLineSegment(sketch, "E204", {"start": v(18.5, -14.87) * mm, "end": v(18.5, -19.86) * mm});
            skLineSegment(sketch, "E205", {"start": v(18.5, -19.86) * mm, "end": v(23.5, -19.86) * mm});
            skLineSegment(sketch, "E206.trimOffspring", {"start": v(18.5, -19.86) * mm, "end": v(21.5, -19.86) * mm, "construction": true});
            skLineSegment(sketch, "E207.bottom", {"start": v(-25.5, 25.14) * mm, "end": v(23.5, 25.14) * mm, "construction": true});
            skLineSegment(sketch, "E207.top", {"start": v(-25.5, -0.35) * mm, "end": v(5.42, -0.35) * mm, "construction": true});
            skLineSegment(sketch, "E207.left", {"start": v(-25.5, 25.14) * mm, "end": v(-25.5, -0.35) * mm, "construction": true});
            skLineSegment(sketch, "E207.right", {"start": v(23.5, 25.14) * mm, "end": v(23.5, -0.35) * mm, "construction": true});
            skLineSegment(sketch, "E208", {"start": v(-23.5, 25.14) * mm, "end": v(-25.5, -0.35) * mm});
            skLineSegment(sketch, "E209", {"start": v(21.5, 25.14) * mm, "end": v(23.5, -0.35) * mm});
            skLineSegment(sketch, "E210.top", {"start": v(-23.5, 29.14) * mm, "end": v(21.5, 29.14) * mm, "construction": true});
            skLineSegment(sketch, "E210.left", {"start": v(-23.5, 25.14) * mm, "end": v(-23.5, 29.14) * mm, "construction": true});
            skLineSegment(sketch, "E210.right", {"start": v(21.5, 25.14) * mm, "end": v(21.5, 29.14) * mm, "construction": true});
            skLineSegment(sketch, "E211", {"start": v(-23.5, 25.14) * mm, "end": v(-19.5, 29.14) * mm});
            skLineSegment(sketch, "E212", {"start": v(21.5, 25.14) * mm, "end": v(17.49, 29.14) * mm});
            skLineSegment(sketch, "E213", {"start": v(17.49, 29.14) * mm, "end": v(-19.94, 29.14) * mm});
            skLineSegment(sketch, "E214.trimOffspring", {"start": v(17.5, 25.14) * mm, "end": v(21.5, 25.14) * mm, "construction": true});
            skLineSegment(sketch, "E215", {"start": v(10.85, -5.79) * mm, "end": v(13.85, -8.79) * mm});
            skLineSegment(sketch, "E216", {"start": v(13.85, -8.79) * mm, "end": v(13.85, -14.87) * mm});
            skLineSegment(sketch, "E217.trimOffspring", {"start": v(10.85, -0.35) * mm, "end": v(23.5, -0.35) * mm, "construction": true});
            skLineSegment(sketch, "E218", {"start": v(13.85, -8.79) * mm, "end": v(10.87, -5.81) * mm});
            skLineSegment(sketch, "E219", {"start": v(10.87, -5.81) * mm, "end": v(10.85, -0.35) * mm});
            skLineSegment(sketch, "E220", {"start": v(10.85, -0.35) * mm, "end": v(5.42, -0.35) * mm});
            skLineSegment(sketch, "E221", {"start": v(5.42, -0.35) * mm, "end": v(0.42, 4.65) * mm});
            skLineSegment(sketch, "E222.bottom", {"start": v(-1, 6.06) * mm, "end": v(-2.41, 6.06) * mm, "construction": true});
            skLineSegment(sketch, "E222.top", {"start": v(-1, 4.65) * mm, "end": v(-2.41, 4.65) * mm, "construction": true});
            skLineSegment(sketch, "E222.left", {"start": v(-1, 6.06) * mm, "end": v(-1, 4.65) * mm, "construction": true});
            skLineSegment(sketch, "E222.right", {"start": v(-2.41, 6.06) * mm, "end": v(-2.41, 4.65) * mm, "construction": true});
            skLineSegment(sketch, "E223.bottom", {"start": v(-1, 6.06) * mm, "end": v(0.42, 6.06) * mm, "construction": true});
            skLineSegment(sketch, "E223.top", {"start": v(-1, 4.65) * mm, "end": v(0.42, 4.65) * mm, "construction": true});
            skLineSegment(sketch, "E223.right", {"start": v(0.42, 6.06) * mm, "end": v(0.42, 4.65) * mm, "construction": true});
            skLineSegment(sketch, "E224.bottom", {"start": v(-2.41, 6.06) * mm, "end": v(0.42, 6.06) * mm, "construction": true});
            skLineSegment(sketch, "E224.top", {"start": v(-2.41, 21.04) * mm, "end": v(0.42, 21.04) * mm, "construction": true});
            skLineSegment(sketch, "E224.left", {"start": v(-2.41, 6.06) * mm, "end": v(-2.41, 21.04) * mm, "construction": true});
            skLineSegment(sketch, "E224.right", {"start": v(0.42, 6.06) * mm, "end": v(0.42, 21.04) * mm, "construction": true});
            skLineSegment(sketch, "E225.bottom", {"start": v(0.42, 21.04) * mm, "end": v(-2.41, 21.04) * mm, "construction": true});
            skLineSegment(sketch, "E225.top", {"start": v(0.42, 29.14) * mm, "end": v(-2.41, 29.14) * mm, "construction": true});
            skLineSegment(sketch, "E225.left", {"start": v(0.42, 21.04) * mm, "end": v(0.42, 29.14) * mm, "construction": true});
            skLineSegment(sketch, "E225.right", {"start": v(-2.41, 21.04) * mm, "end": v(-2.41, 29.14) * mm, "construction": true});
            skLineSegment(sketch, "E226", {"start": v(-1, 29.14) * mm, "end": v(-1, 21.04) * mm});
            skLineSegment(sketch, "E227", {"start": v(-1, 21.04) * mm, "end": v(-1, 6.06) * mm});
            skLineSegment(sketch, "E228", {"start": v(-1, 6.06) * mm, "end": v(-2.41, 6.06) * mm});
            skLineSegment(sketch, "E229", {"start": v(-2.41, 6.06) * mm, "end": v(-2.41, 4.65) * mm});
            skLineSegment(sketch, "E230", {"start": v(-1, 6.06) * mm, "end": v(0.42, 6.06) * mm});
            skLineSegment(sketch, "E231", {"start": v(0.42, 6.06) * mm, "end": v(0.42, 4.65) * mm});
            skSolve(sketch);
        }
        {
            var Q0;
            Q0=makeQuery(id+"F0.imprint","IMPRINT",FACE,{"disambiguationData":[TD([[makeQuery(id+"F0.imprint","IMPRINT",EDGE,{"derivedFrom":sQuery(id+"F0.wireOp",EDGE,"E19")}),1.0]])]});
            var Q1;
            Q1=makeQuery(id+"F0.imprint","IMPRINT",FACE,{"disambiguationData":[TD([[makeQuery(id+"F0.imprint","IMPRINT",EDGE,{"derivedFrom":sQuery(id+"F0.wireOp",EDGE,"E23")}),-1.0]])]});
            extrude(context, id + "F1", {"entities" : qUnion([Q0, Q1]), "depth" : 1050 * mm, "offsetDistance" : 25 * mm, "symmetric" : true});
        }
        {
            var Q0;
            Q0=makeQuery(id+"F0.imprint","IMPRINT",FACE,{"disambiguationData":[TD([[makeQuery(id+"F0.imprint","IMPRINT",EDGE,{"derivedFrom":sQuery(id+"F0.wireOp",EDGE,"E13")}),-1.0]])]});
            extrude(context, id + "F2", {"entities" : qUnion([Q0]), "depth" : 1100 * mm, "offsetDistance" : 25 * mm, "symmetric" : true});
        }
        {
            var Q0;
            Q0=makeQuery(id+"F0.imprint","IMPRINT",FACE,{"disambiguationData":[TD([[makeQuery(id+"F0.imprint","IMPRINT",EDGE,{"derivedFrom":sQuery(id+"F0.wireOp",EDGE,"E68")}),1.0]])]});
            extrude(context, id + "F3", {"entities" : qUnion([Q0]), "operationType" : NewBodyOperationType.ADD, "depth" : 1150 * mm, "offsetDistance" : 25 * mm, "symmetric" : true});
        }
        {
            var Q0;
            Q0=makeQuery(id+"F2.opExtrude","SWEPT_BODY",BODY,{"disambiguationData":[OSD([sQuery(id+"F0.wireOp",EDGE,"E13"),sQuery(id+"F0.wireOp",EDGE,"E14"),sQuery(id+"F0.wireOp",EDGE,"E15"),sQuery(id+"F0.wireOp",EDGE,"E16"),sQuery(id+"F0.wireOp",EDGE,"E17"),sQuery(id+"F0.wireOp",EDGE,"E18"),sQuery(id+"F0.wireOp",EDGE,"E22"),sQuery(id+"F0.wireOp",EDGE,"E26"),sQuery(id+"F0.wireOp",EDGE,"E39"),sQuery(id+"F0.wireOp",EDGE,"E37"),sQuery(id+"F0.wireOp",EDGE,"E40"),sQuery(id+"F0.wireOp",EDGE,"E99"),sQuery(id+"F0.wireOp",EDGE,"E102"),sQuery(id+"F0.wireOp",EDGE,"E105")])]});
            deleteBodies(context, id + "F4", {"entities" : qUnion([Q0])});
        }
        {
            var Q0;
            Q0=makeQuery(id+"F0.imprint","IMPRINT",FACE,{"disambiguationData":[TD([[makeQuery(id+"F0.imprint","IMPRINT",EDGE,{"derivedFrom":sQuery(id+"F0.wireOp",EDGE,"E13")}),-1.0]])]});
            extrude(context, id + "F5", {"entities" : qUnion([Q0]), "depth" : 1100 * mm, "offsetDistance" : 25 * mm, "symmetric" : true});
        }
        {
            var Q0;
            Q0=makeQuery(id+"F0.imprint","IMPRINT",FACE,{"disambiguationData":[TD([[makeQuery(id+"F0.imprint","IMPRINT",EDGE,{"derivedFrom":sQuery(id+"F0.wireOp",EDGE,"E68")}),1.0]])]});
            extrude(context, id + "F6", {"entities" : qUnion([Q0]), "operationType" : NewBodyOperationType.ADD, "depth" : 1150 * mm, "offsetDistance" : 25 * mm, "symmetric" : true});
        }
    });
